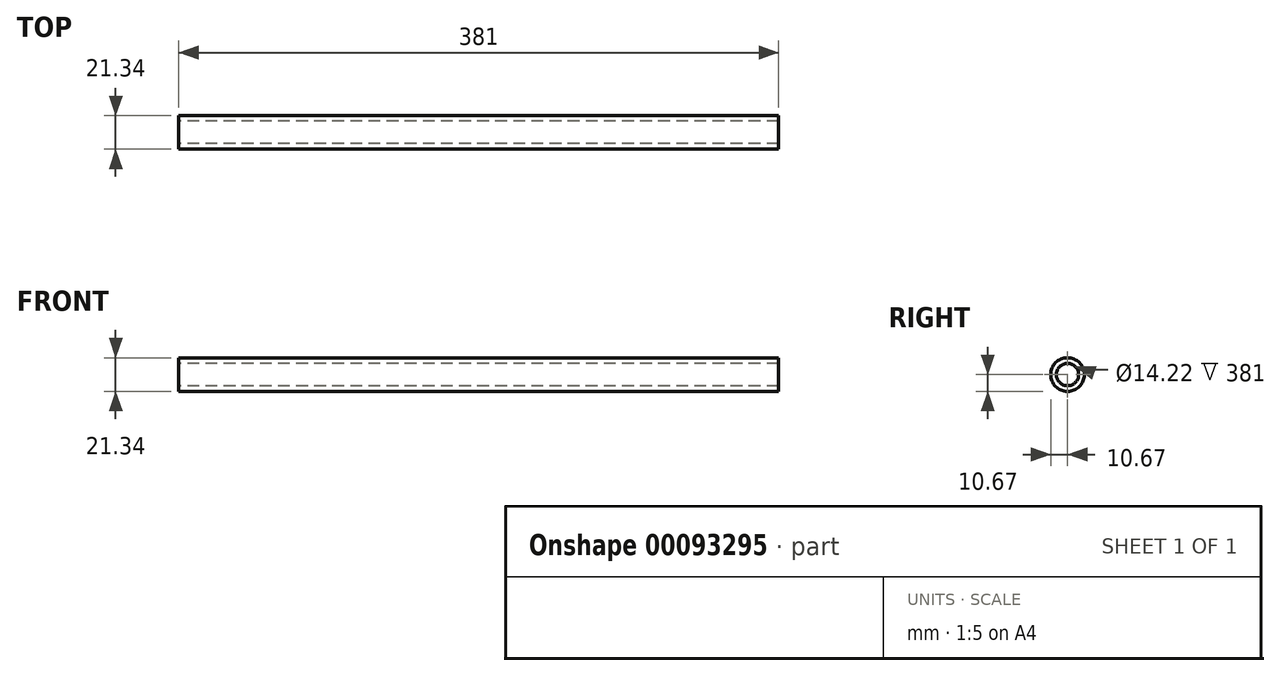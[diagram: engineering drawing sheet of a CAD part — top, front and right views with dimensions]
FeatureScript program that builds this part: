
annotation { "Feature Type Name" : "Feature", "Feature Type Description" : "" }
export const myFeature = defineFeature(function(context is Context, id is Id, definition is map)
    precondition{}
    {
        {
            var Q0;
            Q0=qCreatedBy(makeId("Right.planeOp"),FACE);
            var sketch = newSketch(context, id + "F0", { "sketchPlane" : qUnion([Q0])});
            skCircle(sketch, "E0", {"center": v(0, 0) * mm, "radius": 10.67 * mm});
            skCircle(sketch, "E1", {"center": v(0, 0) * mm, "radius": 7.11 * mm});
            skSolve(sketch);
        }
        {
            var Q0;
            Q0 = qSketchRegion(id + "F0", true);
            extrude(context, id + "F1", {"entities" : qUnion([Q0]), "depth" : 381 * mm});
        }
    });
